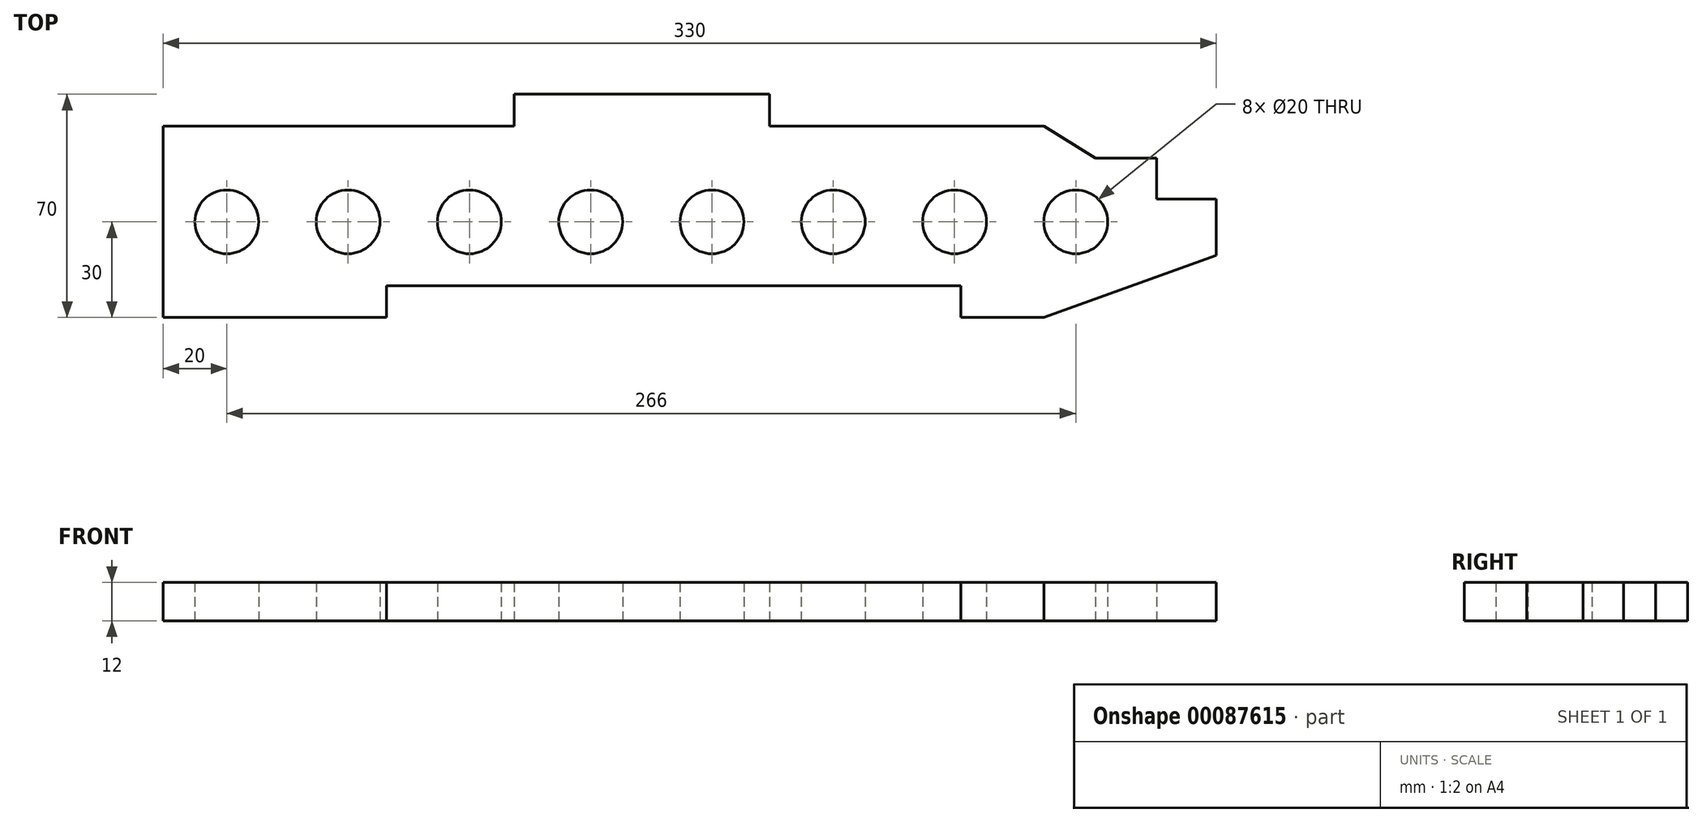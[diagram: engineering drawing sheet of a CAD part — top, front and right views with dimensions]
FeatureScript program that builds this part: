
annotation { "Feature Type Name" : "Feature", "Feature Type Description" : "" }
export const myFeature = defineFeature(function(context is Context, id is Id, definition is map)
    precondition{}
    {
        {
            var Q0;
            Q0=qCreatedBy(makeId("Top.planeOp"),FACE);
            var sketch = newSketch(context, id + "F0", { "sketchPlane" : qUnion([Q0])});
            skLineSegment(sketch, "E0", {"start": v(0, 0) * mm, "end": v(70, 0) * mm});
            skLineSegment(sketch, "E1", {"start": v(70, 0) * mm, "end": v(70, 10) * mm});
            skLineSegment(sketch, "E2", {"start": v(70, 10) * mm, "end": v(250, 10) * mm});
            skLineSegment(sketch, "E3", {"start": v(250, 10) * mm, "end": v(250, 0) * mm});
            skLineSegment(sketch, "E4", {"start": v(250, 0) * mm, "end": v(276.01, 0) * mm});
            skLineSegment(sketch, "E5", {"start": v(276.01, 0) * mm, "end": v(330, 19.53) * mm});
            skLineSegment(sketch, "E6", {"start": v(330, 19.53) * mm, "end": v(330, 37.2) * mm});
            skLineSegment(sketch, "E7", {"start": v(330, 37.2) * mm, "end": v(311.32, 37.2) * mm});
            skLineSegment(sketch, "E8", {"start": v(311.32, 37.2) * mm, "end": v(311.32, 50) * mm});
            skLineSegment(sketch, "E9", {"start": v(311.32, 50) * mm, "end": v(292.12, 50) * mm});
            skLineSegment(sketch, "E10", {"start": v(292.12, 50) * mm, "end": v(276.01, 60) * mm});
            skLineSegment(sketch, "E11", {"start": v(276.01, 60) * mm, "end": v(190, 60) * mm});
            skLineSegment(sketch, "E12", {"start": v(190, 70) * mm, "end": v(190, 60) * mm});
            skLineSegment(sketch, "E13", {"start": v(190, 70) * mm, "end": v(110, 70) * mm});
            skLineSegment(sketch, "E14", {"start": v(110, 60) * mm, "end": v(110, 70) * mm});
            skLineSegment(sketch, "E15", {"start": v(110, 60) * mm, "end": v(0, 60) * mm});
            skLineSegment(sketch, "E16", {"start": v(0, 60) * mm, "end": v(0, 0) * mm});
            skCircle(sketch, "E17", {"center": v(20, 30) * mm, "radius": 10 * mm});
            skCircle(sketch, "E18.1.0.0", {"center": v(58, 30) * mm, "radius": 10 * mm});
            skCircle(sketch, "E18.2.0.0", {"center": v(96, 30) * mm, "radius": 10 * mm});
            skCircle(sketch, "E18.3.0.0", {"center": v(134, 30) * mm, "radius": 10 * mm});
            skCircle(sketch, "E18.4.0.0", {"center": v(172, 30) * mm, "radius": 10 * mm});
            skCircle(sketch, "E18.5.0.0", {"center": v(210, 30) * mm, "radius": 10 * mm});
            skCircle(sketch, "E18.6.0.0", {"center": v(248, 30) * mm, "radius": 10 * mm});
            skCircle(sketch, "E18.7.0.0", {"center": v(286, 30) * mm, "radius": 10 * mm});
            skLineSegment(sketch, "E18.direction1", {"start": v(20, 30) * mm, "end": v(58, 30) * mm, "construction": true});
            skSolve(sketch);
        }
        {
            var Q0;
            Q0 = qSketchRegion(id + "F0", true);
            extrude(context, id + "F1", {"entities" : qUnion([Q0]), "depth" : 12 * mm});
        }
    });
